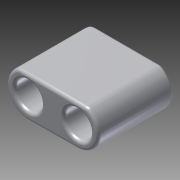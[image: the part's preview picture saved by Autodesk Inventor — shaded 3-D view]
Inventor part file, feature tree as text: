
AUTODESK INVENTOR PART (.ipt)
format: ipt  version: 2015 (Build 190159000, 159)  size: 209,408 bytes
history: native  units: mm
features: extrude x2, sketch x2, fillet x1
ambient origin geometry x8: Origin, YZ Plane, XZ Plane, XY Plane, X Axis, Y Axis, Z Axis, Center Point
bodies: Body1 (feature_tree)
feature tree (5):
  extrude  "Extrusión6"  Depth=1.7mm
  extrude  "Extrusión7"  Depth=0.2mm
  fillet  "Empalme2"  Radius=3.118675mm
  sketch  "Boceto6"  dims[d22=90.0deg d23=1.7mm]
  sketch  "Boceto7"  dims[d24=1.7mm d25=3.118675mm d26=3.118675mm d29=4.1mm d30=4.8mm d31=0.0mm d32=0.2mm d34=1.359338mm d35=1.2mm d36=10.0mm d37=0.0mm d38=0.2mm d39=0.5mm]
